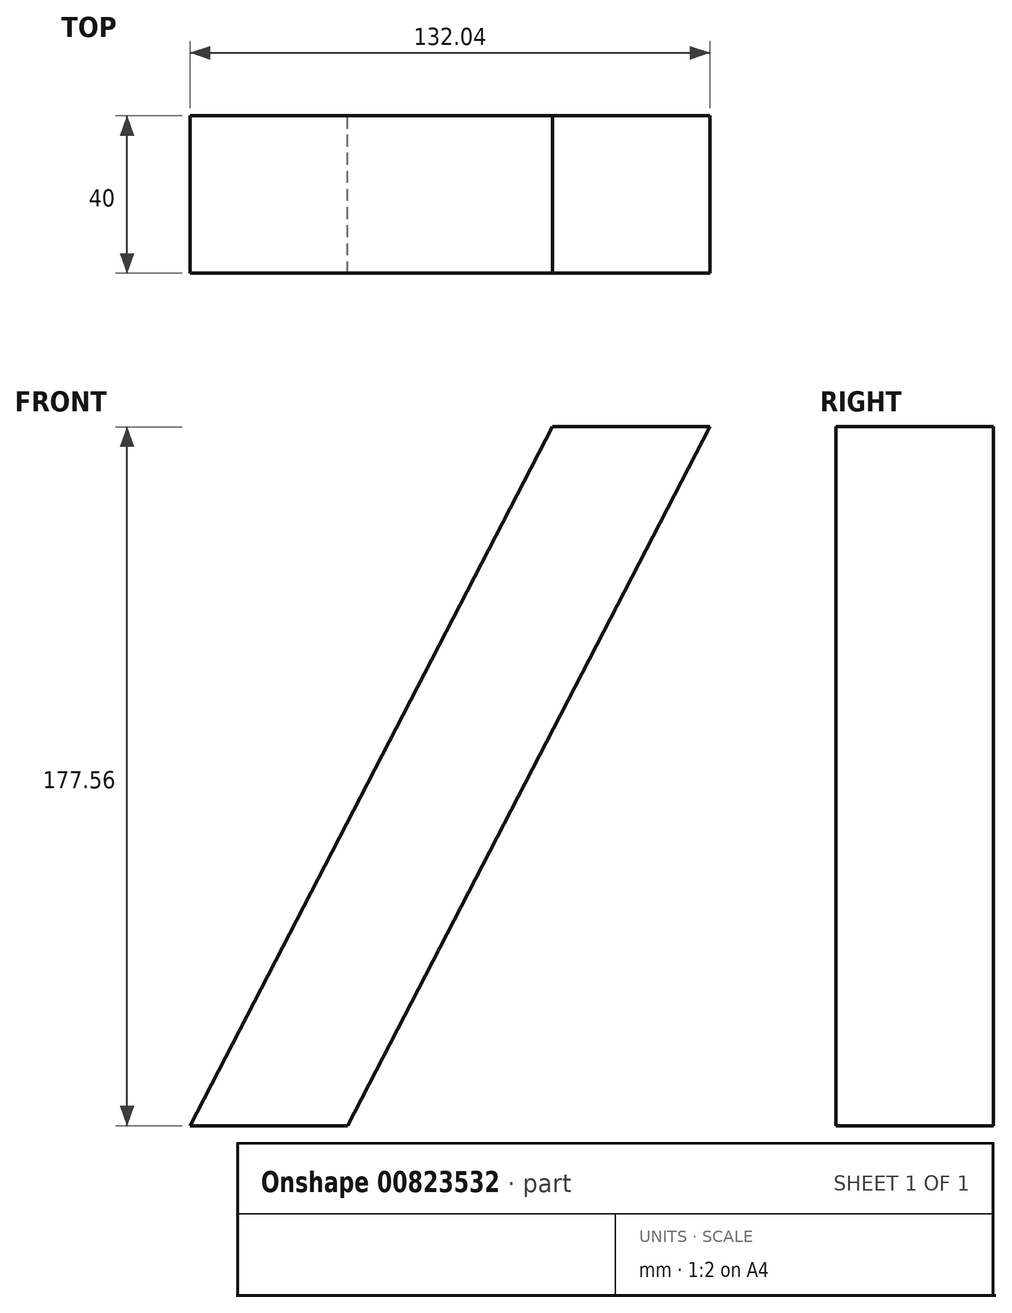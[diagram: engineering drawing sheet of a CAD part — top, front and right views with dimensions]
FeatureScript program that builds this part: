
annotation { "Feature Type Name" : "Feature", "Feature Type Description" : "" }
export const myFeature = defineFeature(function(context is Context, id is Id, definition is map)
    precondition{}
    {
        {
            var Q0;
            Q0=qCreatedBy(makeId("Top.planeOp"),FACE);
            var sketch = newSketch(context, id + "F0", { "sketchPlane" : qUnion([Q0])});
            skLineSegment(sketch, "E0.bottom", {"start": v(20, -20) * mm, "end": v(-20, -20) * mm});
            skLineSegment(sketch, "E0.top", {"start": v(20, 20) * mm, "end": v(-20, 20) * mm});
            skLineSegment(sketch, "E0.left", {"start": v(20, -20) * mm, "end": v(20, 20) * mm});
            skLineSegment(sketch, "E0.right", {"start": v(-20, -20) * mm, "end": v(-20, 20) * mm});
            skPoint(sketch, "E0.middle", {"position": v(0, 0) * mm});
            skSolve(sketch);
        }
        {
            var Q0;
            Q0=qCreatedBy(makeId("Front.planeOp"),FACE);
            var sketch = newSketch(context, id + "F1", { "sketchPlane" : qUnion([Q0])});
            skLineSegment(sketch, "E1", {"start": v(0, 0) * mm, "end": v(92.04, 177.56) * mm});
            skSolve(sketch);
        }
        {
            var Q0;
            Q0=makeQuery(id+"F0.imprint","IMPRINT",FACE,{"disambiguationData":[TD([[makeQuery(id+"F0.imprint","IMPRINT",EDGE,{"derivedFrom":sQuery(id+"F0.wireOp",EDGE,"E0.bottom")}),-1.0]])]});
            var Q1;
            Q1=sQuery(id+"F1.wireOp",EDGE,"E1");
            sweep(context, id + "F2", {"profiles" : qUnion([Q0]), "path" : qUnion([Q1])});
        }
    });
